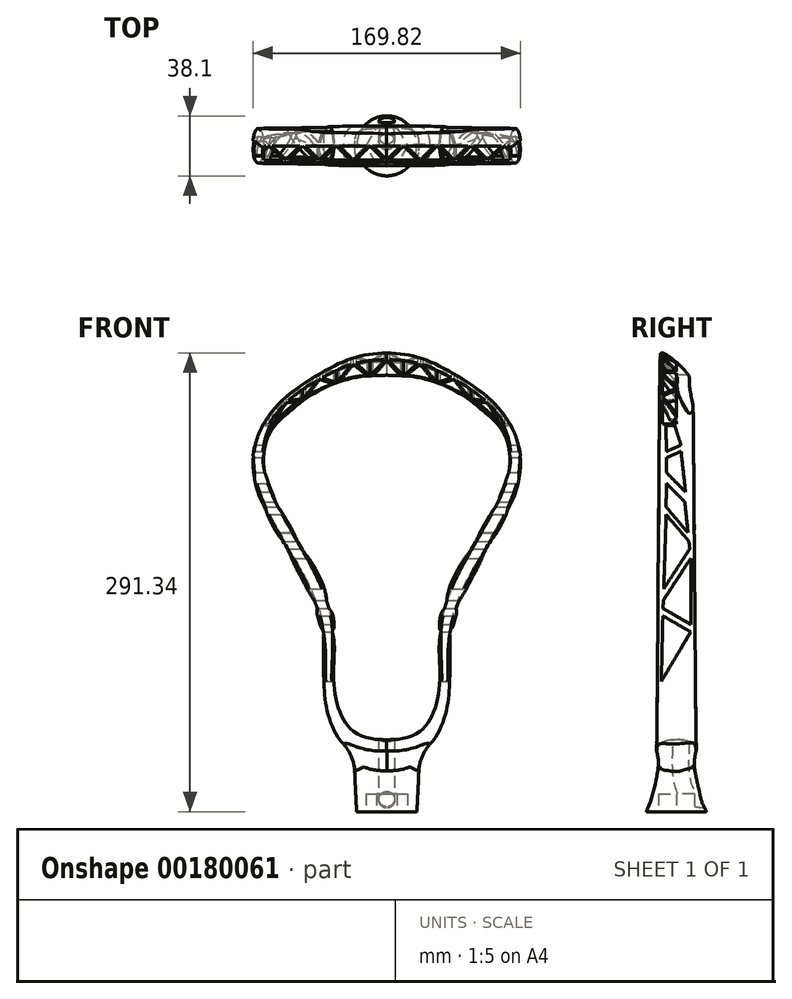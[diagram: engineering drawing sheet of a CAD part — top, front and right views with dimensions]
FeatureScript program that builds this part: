
annotation { "Feature Type Name" : "Feature", "Feature Type Description" : "" }
export const myFeature = defineFeature(function(context is Context, id is Id, definition is map)
    precondition{}
    {
        {
            var Q0;
            Q0=qCreatedBy(makeId("Front.planeOp"),FACE);
            var sketch = newSketch(context, id + "F0", { "sketchPlane" : qUnion([Q0])});
            skFitSpline(sketch, "E0", {"points": [v(0, 133.16) * mm, v(38.53, 123.96) * mm, v(74.69, 98) * mm, v(84.6, 61.8) * mm, v(62.01, 10.45) * mm, v(41.74, -37.17) * mm, v(39.37, -79) * mm, v(29.1, -107.6) * mm, v(0, -119.33) * mm], "startDerivative": vector(423.47, 0) * mm, "endDerivative": vector(-415.85, 0) * mm});
            skLineSegment(sketch, "E1", {"start": v(50.46, 17.85) * mm, "end": v(71.91, 4.1) * mm, "construction": true});
            skLineSegment(sketch, "E2", {"start": v(0, 133.16) * mm, "end": v(0, -119.33) * mm, "construction": true});
            skSolve(sketch);
        }
        {
            var Q0;
            Q0=qCreatedBy(makeId("Right.planeOp"),FACE);
            var sketch = newSketch(context, id + "F1", { "sketchPlane" : qUnion([Q0])});
            skEllipse(sketch, "E3", {"center": v(0, 128.78) * mm, "majorRadius": 14.01 * mm, "minorRadius": 3.18 * mm, "majorAxis": v(-0.7, 0.7)});
            skLineSegment(sketch, "E4", {"start": v(0, 128.78) * mm, "end": v(-9.9, 138.69) * mm, "construction": true});
            skLineSegment(sketch, "E5", {"start": v(0, 128.78) * mm, "end": v(-12.95, 128.78) * mm, "construction": true});
            skEllipse(sketch, "E6", {"center": v(0, -112.98) * mm, "majorRadius": 12.7 * mm, "minorRadius": 6.35 * mm, "majorAxis": v(1, 0)});
            skLineSegment(sketch, "E7", {"start": v(0, 140.7) * mm, "end": v(0, 110.5) * mm, "construction": true});
            skLineSegment(sketch, "E8", {"start": v(10.16, 144.05) * mm, "end": v(10.16, 100.57) * mm, "construction": true});
            skSolve(sketch);
        }
        {
            var Q0;
            Q0=sQuery(id+"F0.wireOp",EDGE,"E1");
            var Q1;
            Q1=qCreatedBy(makeId("Front.planeOp"),FACE);
            cPlane(context, id + "F2", {"entities" : qUnion([Q0, Q1]), "cplaneType" : CPlaneType.LINE_ANGLE, "offset" : 25.4 * mm, "angle" : 90 * degree, "width" : 152.4 * mm, "height" : 152.4 * mm});
        }
        {
            var Q0;
            Q0=qCreatedBy(id+"F2.planeOp",FACE);
            var sketch = newSketch(context, id + "F3", { "sketchPlane" : qUnion([Q0])});
            skEllipse(sketch, "E9", {"center": v(41.5, 0) * mm, "majorRadius": 11.43 * mm, "minorRadius": 5.08 * mm, "majorAxis": v(0, 1)});
            skSolve(sketch);
        }
        {
            var Q0;
            Q0=makeQuery(id+"F1.imprint","IMPRINT",FACE,{"disambiguationData":[TD([[makeQuery(id+"F1.imprint","IMPRINT",EDGE,{"derivedFrom":sQuery(id+"F1.wireOp",EDGE,"E3")}),1.0]])]});
            var Q1;
            Q1=makeQuery(id+"F3.imprint","IMPRINT",FACE,{"disambiguationData":[TD([[makeQuery(id+"F3.imprint","IMPRINT",EDGE,{"derivedFrom":sQuery(id+"F3.wireOp",EDGE,"E9")}),1.0]])]});
            var Q2;
            Q2=makeQuery(id+"F1.imprint","IMPRINT",FACE,{"disambiguationData":[TD([[makeQuery(id+"F1.imprint","IMPRINT",EDGE,{"derivedFrom":sQuery(id+"F1.wireOp",EDGE,"E6")}),1.0]])]});
            var Q3;
            Q3=sQuery(id+"F0.wireOp",EDGE,"E0");
            loft(context, id + "F4", {"addGuides" : true, "sheetProfilesArray" : [{ "sheetProfileEntities" : qUnion([Q0]) }, { "sheetProfileEntities" : qUnion([Q1]) }, { "sheetProfileEntities" : qUnion([Q2]) }], "guidesArray" : [{ "guideEntities" : qUnion([Q3]), "guideDerivativeType" : LoftGuideDerivativeType.DEFAULT, "guideDerivativeMagnitude" : 1 }]});
        }
        {
            var Q0;
            Q0=makeQuery(id+"F4.opLoft","SWEPT_BODY",BODY,{"disambiguationData":[OSD([sQuery(id+"F0.wireOp",EDGE,"E0"),makeQuery(id+"F1.imprint","IMPRINT",FACE,{"disambiguationData":[TD([[makeQuery(id+"F1.imprint","IMPRINT",EDGE,{"derivedFrom":sQuery(id+"F1.wireOp",EDGE,"E3")}),1.0]])]}),makeQuery(id+"F1.imprint","IMPRINT",FACE,{"disambiguationData":[TD([[makeQuery(id+"F1.imprint","IMPRINT",EDGE,{"derivedFrom":sQuery(id+"F1.wireOp",EDGE,"E6")}),1.0]])]}),sQuery(id+"F3.wireOp",EDGE,"E9")])]});
            var Q1;
            Q1=qCreatedBy(makeId("Right.planeOp"),FACE);
            mirror(context, id + "F5", {"operationType" : NewBodyOperationType.ADD, "entities" : qUnion([Q0]), "mirrorPlane" : qUnion([Q1])});
        }
        {
            var Q0;
            Q0=qCreatedBy(makeId("Front.planeOp"),FACE);
            var sketch = newSketch(context, id + "F6", { "sketchPlane" : qUnion([Q0])});
            skFitSpline(sketch, "E10", {"points": [v(-65.6, 98.25) * mm, v(-46.52, 113.2) * mm, v(-22.04, 122.89) * mm, v(0, 124.8) * mm], "startDerivative": vector(53.63, 47.73) * mm, "endDerivative": vector(67.97, 1.48) * mm});
            skFitSpline(sketch, "E11.MirrorCS", {"points": [v(65.6, 98.25) * mm, v(46.52, 113.2) * mm, v(22.04, 122.89) * mm, v(0, 124.8) * mm], "startDerivative": vector(-53.63, 47.73) * mm, "endDerivative": vector(-67.97, 1.48) * mm});
            skLineSegment(sketch, "E12", {"start": v(-65.6, 98.25) * mm, "end": v(65.6, 98.25) * mm});
            skSolve(sketch);
        }
        {
            var Q0;
            Q0 = qSketchRegion(id + "F6", true);
            extrude(context, id + "F7", {"entities" : qUnion([Q0]), "operationType" : NewBodyOperationType.REMOVE, "oppositeDirection" : true, "depth" : 45.72 * mm, "symmetric" : true});
        }
        {
            var Q0;
            Q0=makeQuery(id+"F7.boolean.opBoolean","COPY",EDGE,{"derivedFrom":makeQuery(id+"F7.opExtrude","SWEPT_EDGE",EDGE,{"disambiguationData":[OSD([sQuery(id+"F6.wireOp",EDGE,"E10"),sQuery(id+"F6.wireOp",EDGE,"E11.MirrorCS")])]})});
            fillet(context, id + "F8", {"entities" : qUnion([Q0]), "radius" : 2.54 * mm, "tangentPropagation" : true, "allowEdgeOverflow" : false});
        }
        {
            var Q0;
            Q0=qCreatedBy(makeId("Right.planeOp"),FACE);
            var sketch = newSketch(context, id + "F9", { "sketchPlane" : qUnion([Q0])});
            skLineSegment(sketch, "E13", {"start": v(-9.55, -69.61) * mm, "end": v(9.13, -38.22) * mm});
            skLineSegment(sketch, "E14", {"start": v(5.33, 44.3) * mm, "end": v(-6.29, 56.08) * mm});
            skLineSegment(sketch, "E15", {"start": v(-6.29, 56.08) * mm, "end": v(-6.55, 41.14) * mm});
            skLineSegment(sketch, "E16", {"start": v(-6.84, 24.52) * mm, "end": v(-8.04, -10.87) * mm});
            skLineSegment(sketch, "E17", {"start": v(-9.55, -69.61) * mm, "end": v(-8.63, -28.02) * mm});
            skLineSegment(sketch, "E18", {"start": v(9.13, -33.47) * mm, "end": v(9.13, 8.56) * mm});
            skLineSegment(sketch, "E19", {"start": v(5.33, 44.3) * mm, "end": v(7.4, 24.82) * mm});
            skLineSegment(sketch, "E20", {"start": v(-8.63, -28.02) * mm, "end": v(9.13, -38.22) * mm});
            skLineSegment(sketch, "E21", {"start": v(-8.47, -23.36) * mm, "end": v(9.13, -33.47) * mm});
            skLineSegment(sketch, "E22", {"start": v(-8.3, -18.19) * mm, "end": v(9.13, 8.56) * mm});
            skLineSegment(sketch, "E23", {"start": v(-8.04, -10.87) * mm, "end": v(8.5, 14.53) * mm});
            skLineSegment(sketch, "E24", {"start": v(8, 19.26) * mm, "end": v(-6.64, 36.37) * mm});
            skLineSegment(sketch, "E25", {"start": v(7.4, 24.82) * mm, "end": v(-6.55, 41.14) * mm});
            skLineSegment(sketch, "E26.trimOffspring", {"start": v(-8.3, -18.19) * mm, "end": v(-8.47, -23.36) * mm});
            skLineSegment(sketch, "E27.trimOffspring", {"start": v(8, 19.26) * mm, "end": v(8.5, 14.53) * mm});
            skLineSegment(sketch, "E28.trimOffspring", {"start": v(-6.64, 36.37) * mm, "end": v(-6.84, 24.52) * mm});
            skLineSegment(sketch, "E29", {"start": v(5.83, 50.65) * mm, "end": v(-6.29, 62.93) * mm});
            skLineSegment(sketch, "E30", {"start": v(-6.29, 62.93) * mm, "end": v(-6.29, 72.4) * mm});
            skLineSegment(sketch, "E31", {"start": v(-6.29, 72.4) * mm, "end": v(2.95, 76.46) * mm});
            skLineSegment(sketch, "E32", {"start": v(2.95, 76.46) * mm, "end": v(5.83, 50.65) * mm});
            skLineSegment(sketch, "E33", {"start": v(-6.29, 76.4) * mm, "end": v(2.95, 80.44) * mm});
            skLineSegment(sketch, "E34", {"start": v(2.95, 80.44) * mm, "end": v(-1.04, 92.76) * mm});
            skLineSegment(sketch, "E35", {"start": v(-1.04, 92.76) * mm, "end": v(-6.65, 92.76) * mm});
            skLineSegment(sketch, "E36", {"start": v(-6.65, 92.76) * mm, "end": v(-6.29, 76.4) * mm});
            skSolve(sketch);
        }
        {
            var Q0;
            Q0=makeQuery(id+"F9.imprint","IMPRINT",FACE,{"disambiguationData":[TD([[makeQuery(id+"F9.imprint","IMPRINT",EDGE,{"derivedFrom":sQuery(id+"F9.wireOp",EDGE,"E13")}),1.0]])]});
            var Q1;
            Q1=makeQuery(id+"F9.imprint","IMPRINT",FACE,{"disambiguationData":[TD([[makeQuery(id+"F9.imprint","IMPRINT",EDGE,{"derivedFrom":sQuery(id+"F9.wireOp",EDGE,"E14")}),1.0]])]});
            var Q2;
            Q2=makeQuery(id+"F9.imprint","IMPRINT",FACE,{"disambiguationData":[TD([[makeQuery(id+"F9.imprint","IMPRINT",EDGE,{"derivedFrom":sQuery(id+"F9.wireOp",EDGE,"E16")}),1.0]])]});
            var Q3;
            Q3=makeQuery(id+"F9.imprint","IMPRINT",FACE,{"disambiguationData":[TD([[makeQuery(id+"F9.imprint","IMPRINT",EDGE,{"derivedFrom":sQuery(id+"F9.wireOp",EDGE,"E18")}),1.0]])]});
            var Q4;
            Q4=makeQuery(id+"F9.imprint","IMPRINT",FACE,{"disambiguationData":[TD([[makeQuery(id+"F9.imprint","IMPRINT",EDGE,{"derivedFrom":sQuery(id+"F9.wireOp",EDGE,"E29")}),-1.0]])]});
            var Q5;
            Q5=makeQuery(id+"F9.imprint","IMPRINT",FACE,{"disambiguationData":[TD([[makeQuery(id+"F9.imprint","IMPRINT",EDGE,{"derivedFrom":sQuery(id+"F9.wireOp",EDGE,"E33")}),1.0]])]});
            var Q6;
            Q6=makeQuery(id+"F9.imprint","IMPRINT",FACE,{"disambiguationData":[TD([[makeQuery(id+"F9.imprint","IMPRINT",EDGE,{"derivedFrom":sQuery(id+"F9.wireOp",EDGE,"E13")}),1.0]])]});
            extrude(context, id + "F10", {"entities" : qUnion([Q0, Q1, Q2, Q3, Q4, Q5, Q6]), "operationType" : NewBodyOperationType.REMOVE, "oppositeDirection" : true, "depth" : 203.2 * mm, "symmetric" : true});
        }
        {
            var Q0;
            Q0=qCreatedBy(makeId("Top.planeOp"),FACE);
            cPlane(context, id + "F11", {"entities" : qUnion([Q0]), "cplaneType" : CPlaneType.OFFSET, "offset" : 152.4 * mm, "oppositeDirection" : true, "width" : 152.4 * mm, "height" : 152.4 * mm});
        }
        {
            var Q0;
            Q0=qCreatedBy(id+"F11.planeOp",FACE);
            var sketch = newSketch(context, id + "F12", { "sketchPlane" : qUnion([Q0])});
            skCircle(sketch, "E37", {"center": v(0, 0) * mm, "radius": 19.05 * mm});
            skSolve(sketch);
        }
        {
            var Q0;
            Q0=qCreatedBy(id+"F11.planeOp",FACE);
            var Q1;
            Q1=sQuery(id+"F1.wireOp",VERTEX,"E6.center");
            cPlane(context, id + "F13", {"entities" : qUnion([Q0, Q1]), "cplaneType" : CPlaneType.PLANE_POINT, "offset" : 25.4 * mm, "width" : 152.4 * mm, "height" : 152.4 * mm});
        }
        {
            var Q0;
            Q0=qCreatedBy(id+"F13.planeOp",FACE);
            var sketch = newSketch(context, id + "F14", { "sketchPlane" : qUnion([Q0])});
            skLineSegment(sketch, "E38.bottom", {"start": v(14.64, 10.24) * mm, "end": v(-14.64, 10.24) * mm});
            skLineSegment(sketch, "E38.top", {"start": v(14.64, -10.24) * mm, "end": v(-14.64, -10.24) * mm});
            skLineSegment(sketch, "E38.left", {"start": v(20.99, 3.89) * mm, "end": v(20.99, -3.89) * mm});
            skLineSegment(sketch, "E38.right", {"start": v(-20.99, 3.89) * mm, "end": v(-20.99, -3.89) * mm});
            skPoint(sketch, "E38.middle", {"position": v(0, 0) * mm});
            skPoint(sketch, "E39.visualSharp", {"position": v(-20.99, -10.24) * mm});
            skArc(sketch, "E39.filletArc", {"start": v(-20.99, -3.89) * mm, "mid": v(-19.13, -8.38) * mm, "end": v(-14.64, -10.24) * mm});
            skPoint(sketch, "E40.visualSharp", {"position": v(-20.99, 10.24) * mm});
            skArc(sketch, "E40.filletArc", {"start": v(-14.64, 10.24) * mm, "mid": v(-19.13, 8.38) * mm, "end": v(-20.99, 3.89) * mm});
            skPoint(sketch, "E41.visualSharp", {"position": v(20.99, 10.24) * mm});
            skArc(sketch, "E41.filletArc", {"start": v(20.99, 3.89) * mm, "mid": v(19.13, 8.38) * mm, "end": v(14.64, 10.24) * mm});
            skPoint(sketch, "E42.visualSharp", {"position": v(20.99, -10.24) * mm});
            skArc(sketch, "E42.filletArc", {"start": v(14.64, -10.24) * mm, "mid": v(19.13, -8.38) * mm, "end": v(20.99, -3.89) * mm});
            skSolve(sketch);
        }
        {
            var Q0;
            Q0=qCreatedBy(makeId("Right.planeOp"),FACE);
            var sketch = newSketch(context, id + "F15", { "sketchPlane" : qUnion([Q0])});
            skFitSpline(sketch, "E43", {"points": [v(-19.05, -152.4) * mm, v(-10.24, -112.98) * mm], "startDerivative": vector(12.31, 25.97) * mm, "endDerivative": vector(2.23, 40.23) * mm});
            skFitSpline(sketch, "E44.MirrorCS", {"points": [v(19.05, -152.4) * mm, v(10.24, -112.98) * mm], "startDerivative": vector(-12.31, 25.97) * mm, "endDerivative": vector(-2.23, 40.23) * mm});
            skSolve(sketch);
        }
        {
            var Q1;
            Q1=makeQuery(id+"F12.imprint","IMPRINT",FACE,{"disambiguationData":[TD([[makeQuery(id+"F12.imprint","IMPRINT",EDGE,{"derivedFrom":sQuery(id+"F12.wireOp",EDGE,"E37")}),1.0]])]});
            var Q2;
            Q2 = qSketchRegion(id + "F14", true);
            var Q3;
            Q3=sQuery(id+"F15.wireOp",EDGE,"E44.MirrorCS");
            var Q4;
            Q4=sQuery(id+"F15.wireOp",EDGE,"E43");
            loft(context, id + "F16", {"operationType" : NewBodyOperationType.ADD, "addGuides" : true, "sheetProfilesArray" : [{ "sheetProfileEntities" : qUnion([Q1]) }, { "sheetProfileEntities" : qUnion([Q2]) }], "guidesArray" : [{ "guideEntities" : qUnion([Q3]), "guideDerivativeType" : LoftGuideDerivativeType.DEFAULT, "guideDerivativeMagnitude" : 1 }, { "guideEntities" : qUnion([Q4]), "guideDerivativeType" : LoftGuideDerivativeType.DEFAULT, "guideDerivativeMagnitude" : 1 }]});
        }
        {
            var Q0;
            Q0=makeQuery(id+"F16.boolean.opBoolean","INTERSECT",EDGE,{"derivedFrom":[makeQuery(id+"F5.opPattern","COPY",FACE,{"derivedFrom":makeQuery(id+"F4.opLoft","SWEPT_FACE",FACE,{"disambiguationData":[OSD([sQuery(id+"F0.wireOp",EDGE,"E0"),sQuery(id+"F1.wireOp",EDGE,"E3"),sQuery(id+"F3.wireOp",EDGE,"E9")])]}),"instanceName":"1"}),makeQuery(id+"F16.opLoft","SWEPT_FACE",FACE,{"disambiguationData":[OSD([sQuery(id+"F12.wireOp",EDGE,"E37"),sQuery(id+"F14.wireOp",EDGE,"E38.bottom"),sQuery(id+"F14.wireOp",EDGE,"E40.filletArc"),sQuery(id+"F14.wireOp",EDGE,"E41.filletArc")])]})]});
            fillet(context, id + "F17", {"entities" : qUnion([Q0]), "radius" : 27.94 * mm, "tangentPropagation" : true, "allowEdgeOverflow" : false});
        }
        {
            var Q0;
            Q0=makeQuery(id+"F12.imprint","IMPRINT",FACE,{"disambiguationData":[TD([[makeQuery(id+"F12.imprint","IMPRINT",EDGE,{"derivedFrom":sQuery(id+"F12.wireOp",EDGE,"E37")}),1.0]])]});
            var sketch = newSketch(context, id + "F18", { "sketchPlane" : qUnion([Q0])});
            skCircle(sketch, "E45.cCircle", {"center": v(0, 0) * mm, "radius": 11.43 * mm, "construction": true});
            skLineSegment(sketch, "E45.0", {"start": v(6.6, 11.43) * mm, "end": v(13.2, 0) * mm});
            skLineSegment(sketch, "E45.1", {"start": v(13.2, 0) * mm, "end": v(6.6, -11.43) * mm});
            skLineSegment(sketch, "E45.2", {"start": v(6.6, -11.43) * mm, "end": v(-6.6, -11.43) * mm});
            skLineSegment(sketch, "E45.3", {"start": v(-6.6, -11.43) * mm, "end": v(-13.2, 0) * mm});
            skLineSegment(sketch, "E45.4", {"start": v(-13.2, 0) * mm, "end": v(-6.6, 11.43) * mm});
            skLineSegment(sketch, "E45.5", {"start": v(-6.6, 11.43) * mm, "end": v(6.6, 11.43) * mm});
            skPoint(sketch, "E45.0.midPoint", {"position": v(9.9, 5.71) * mm});
            skSolve(sketch);
        }
        {
            var Q0;
            Q0 = qSketchRegion(id + "F18", true);
            extrude(context, id + "F19", {"entities" : qUnion([Q0]), "operationType" : NewBodyOperationType.REMOVE, "depth" : 11.43 * mm});
        }
        {
            var Q0;
            Q0=qCreatedBy(makeId("Top.planeOp"),FACE);
            cPlane(context, id + "F20", {"entities" : qUnion([Q0]), "cplaneType" : CPlaneType.OFFSET, "offset" : 93.98 * mm, "width" : 152.4 * mm, "height" : 152.4 * mm});
        }
        {
            var Q0;
            Q0=qCreatedBy(id+"F20.planeOp",FACE);
            var sketch = newSketch(context, id + "F21", { "sketchPlane" : qUnion([Q0])});
            skLineSegment(sketch, "E46", {"start": v(0, -8.89) * mm, "end": v(-85.49, -8.9) * mm});
            skLineSegment(sketch, "E47", {"start": v(-85.49, -8.9) * mm, "end": v(-85.49, 0) * mm});
            skLineSegment(sketch, "E48", {"start": v(-85.49, 0) * mm, "end": v(0, 0) * mm});
            skLineSegment(sketch, "E49", {"start": v(0, 0) * mm, "end": v(0, -8.89) * mm});
            skLineSegment(sketch, "E50", {"start": v(0, -8.89) * mm, "end": v(-8.9, 0) * mm});
            skLineSegment(sketch, "E51", {"start": v(-1.8, -8.89) * mm, "end": v(-10.69, 0) * mm});
            skLineSegment(sketch, "E52", {"start": v(-12.48, 0) * mm, "end": v(-21.37, -8.89) * mm});
            skLineSegment(sketch, "E53", {"start": v(-19.58, -8.89) * mm, "end": v(-10.69, 0) * mm});
            skLineSegment(sketch, "E54.1.0.0", {"start": v(-21.37, -8.89) * mm, "end": v(-30.26, 0) * mm});
            skLineSegment(sketch, "E54.1.0.1", {"start": v(-23.17, -8.89) * mm, "end": v(-32.06, 0) * mm});
            skLineSegment(sketch, "E54.1.0.2", {"start": v(-40.95, -8.89) * mm, "end": v(-32.06, 0) * mm});
            skLineSegment(sketch, "E54.1.0.3", {"start": v(-33.85, 0) * mm, "end": v(-42.74, -8.89) * mm});
            skLineSegment(sketch, "E54.2.0.0", {"start": v(-42.74, -8.89) * mm, "end": v(-51.63, 0) * mm});
            skLineSegment(sketch, "E54.2.0.1", {"start": v(-44.54, -8.89) * mm, "end": v(-53.43, 0) * mm});
            skLineSegment(sketch, "E54.2.0.2", {"start": v(-62.32, -8.89) * mm, "end": v(-53.43, 0) * mm});
            skLineSegment(sketch, "E54.2.0.3", {"start": v(-55.23, 0) * mm, "end": v(-64.12, -8.89) * mm});
            skLineSegment(sketch, "E54.3.0.0", {"start": v(-64.11, -8.89) * mm, "end": v(-73, 0) * mm});
            skLineSegment(sketch, "E54.3.0.1", {"start": v(-65.91, -8.89) * mm, "end": v(-74.8, 0) * mm});
            skLineSegment(sketch, "E54.3.0.2", {"start": v(-83.7, -8.89) * mm, "end": v(-74.8, 0) * mm});
            skLineSegment(sketch, "E54.3.0.3", {"start": v(-76.6, 0) * mm, "end": v(-85.49, -8.89) * mm});
            skLineSegment(sketch, "E54.direction1", {"start": v(0, -8.89) * mm, "end": v(-21.37, -8.89) * mm, "construction": true});
            skLineSegment(sketch, "E55.MirrorCS", {"start": v(76.6, 0) * mm, "end": v(85.49, -8.89) * mm});
            skLineSegment(sketch, "E56.MirrorCS", {"start": v(64.11, -8.89) * mm, "end": v(73, 0) * mm});
            skLineSegment(sketch, "E57.MirrorCS", {"start": v(83.7, -8.89) * mm, "end": v(74.8, 0) * mm});
            skLineSegment(sketch, "E58.MirrorCS", {"start": v(0, -8.89) * mm, "end": v(21.37, -8.89) * mm, "construction": true});
            skLineSegment(sketch, "E59.MirrorCS", {"start": v(42.74, -8.89) * mm, "end": v(51.63, 0) * mm});
            skLineSegment(sketch, "E60.MirrorCS", {"start": v(33.85, 0) * mm, "end": v(42.74, -8.89) * mm});
            skLineSegment(sketch, "E61.MirrorCS", {"start": v(40.95, -8.89) * mm, "end": v(32.06, 0) * mm});
            skLineSegment(sketch, "E62.MirrorCS", {"start": v(23.17, -8.89) * mm, "end": v(32.06, 0) * mm});
            skLineSegment(sketch, "E63.MirrorCS", {"start": v(21.37, -8.89) * mm, "end": v(30.26, 0) * mm});
            skLineSegment(sketch, "E64.MirrorCS", {"start": v(0, -8.89) * mm, "end": v(85.49, -8.89) * mm});
            skLineSegment(sketch, "E65.MirrorCS", {"start": v(19.58, -8.89) * mm, "end": v(10.69, 0) * mm});
            skLineSegment(sketch, "E66.MirrorCS", {"start": v(62.32, -8.89) * mm, "end": v(53.43, 0) * mm});
            skLineSegment(sketch, "E67.MirrorCS", {"start": v(44.54, -8.89) * mm, "end": v(53.43, 0) * mm});
            skLineSegment(sketch, "E68.MirrorCS", {"start": v(0, -8.89) * mm, "end": v(8.9, 0) * mm});
            skLineSegment(sketch, "E69.MirrorCS", {"start": v(1.8, -8.89) * mm, "end": v(10.69, 0) * mm});
            skLineSegment(sketch, "E70.MirrorCS", {"start": v(12.48, 0) * mm, "end": v(21.37, -8.89) * mm});
            skLineSegment(sketch, "E71.MirrorCS", {"start": v(65.91, -8.89) * mm, "end": v(74.8, 0) * mm});
            skLineSegment(sketch, "E72.MirrorCS", {"start": v(55.23, 0) * mm, "end": v(64.12, -8.89) * mm});
            skLineSegment(sketch, "E73.MirrorCS", {"start": v(85.49, 0) * mm, "end": v(0, 0) * mm});
            skLineSegment(sketch, "E74.MirrorCS", {"start": v(85.49, -8.9) * mm, "end": v(85.49, 0) * mm});
            skSolve(sketch);
        }
        {
            var Q0;
            {var subQ0=sQuery(id+"F21.wireOp",EDGE,"E49");Q0=makeQuery(id+"F21.imprint","IMPRINT",FACE,{"disambiguationData":[TD([[makeQuery(id+"F21.imprint","IMPRINT",EDGE,{"derivedFrom":subQ0}),-1.0]])]});}
            var Q1;
            {var subQ0=sQuery(id+"F21.wireOp",EDGE,"E51");Q1=makeQuery(id+"F21.imprint","IMPRINT",FACE,{"disambiguationData":[TD([[makeQuery(id+"F21.imprint","IMPRINT",EDGE,{"derivedFrom":subQ0}),1.0]])]});}
            var Q2;
            {var subQ0=sQuery(id+"F21.wireOp",EDGE,"E52");var subQ1=sQuery(id+"F21.wireOp",EDGE,"E48");var subQ2=makeQuery(id+"F21.imprint","INTERSECT",VERTEX,{"derivedFrom":[subQ1,subQ0]});Q2=makeQuery(id+"F21.imprint","IMPRINT",FACE,{"disambiguationData":[TD([[makeQuery(id+"F21.imprint","IMPRINT",EDGE,{"disambiguationData":[TD([[subQ2,1.0]])],"derivedFrom":subQ1}),-1.0]])]});}
            var Q3;
            {var subQ0=sQuery(id+"F21.wireOp",EDGE,"E54.1.0.1");Q3=makeQuery(id+"F21.imprint","IMPRINT",FACE,{"disambiguationData":[TD([[makeQuery(id+"F21.imprint","IMPRINT",EDGE,{"derivedFrom":subQ0}),1.0]])]});}
            var Q4;
            {var subQ0=sQuery(id+"F21.wireOp",EDGE,"E54.1.0.3");var subQ1=sQuery(id+"F21.wireOp",EDGE,"E48");var subQ2=makeQuery(id+"F21.imprint","INTERSECT",VERTEX,{"derivedFrom":[subQ1,subQ0]});Q4=makeQuery(id+"F21.imprint","IMPRINT",FACE,{"disambiguationData":[TD([[makeQuery(id+"F21.imprint","IMPRINT",EDGE,{"disambiguationData":[TD([[subQ2,1.0]])],"derivedFrom":subQ1}),-1.0]])]});}
            var Q5;
            {var subQ0=sQuery(id+"F21.wireOp",EDGE,"E54.2.0.1");Q5=makeQuery(id+"F21.imprint","IMPRINT",FACE,{"disambiguationData":[TD([[makeQuery(id+"F21.imprint","IMPRINT",EDGE,{"derivedFrom":subQ0}),1.0]])]});}
            var Q6;
            {var subQ0=sQuery(id+"F21.wireOp",EDGE,"E54.2.0.3");var subQ1=sQuery(id+"F21.wireOp",EDGE,"E48");var subQ2=makeQuery(id+"F21.imprint","INTERSECT",VERTEX,{"derivedFrom":[subQ1,subQ0]});Q6=makeQuery(id+"F21.imprint","IMPRINT",FACE,{"disambiguationData":[TD([[makeQuery(id+"F21.imprint","IMPRINT",EDGE,{"disambiguationData":[TD([[subQ2,1.0]])],"derivedFrom":subQ1}),-1.0]])]});}
            var Q7;
            {var subQ0=sQuery(id+"F21.wireOp",EDGE,"E54.3.0.1");Q7=makeQuery(id+"F21.imprint","IMPRINT",FACE,{"disambiguationData":[TD([[makeQuery(id+"F21.imprint","IMPRINT",EDGE,{"derivedFrom":subQ0}),1.0]])]});}
            var Q8;
            {var subQ0=sQuery(id+"F21.wireOp",EDGE,"E47");Q8=makeQuery(id+"F21.imprint","IMPRINT",FACE,{"disambiguationData":[TD([[makeQuery(id+"F21.imprint","IMPRINT",EDGE,{"derivedFrom":subQ0}),-1.0]])]});}
            var Q9;
            {var subQ0=sQuery(id+"F21.wireOp",EDGE,"E49");Q9=makeQuery(id+"F21.imprint","IMPRINT",FACE,{"disambiguationData":[TD([[makeQuery(id+"F21.imprint","IMPRINT",EDGE,{"derivedFrom":subQ0}),1.0]])]});}
            var Q10;
            {var subQ0=sQuery(id+"F21.wireOp",EDGE,"E65.MirrorCS");Q10=makeQuery(id+"F21.imprint","IMPRINT",FACE,{"disambiguationData":[TD([[makeQuery(id+"F21.imprint","IMPRINT",EDGE,{"derivedFrom":subQ0}),1.0]])]});}
            var Q11;
            {var subQ0=sQuery(id+"F21.wireOp",EDGE,"E73.MirrorCS");var subQ1=sQuery(id+"F21.wireOp",EDGE,"E63.MirrorCS");var subQ2=makeQuery(id+"F21.imprint","INTERSECT",VERTEX,{"derivedFrom":[subQ1,subQ0]});Q11=makeQuery(id+"F21.imprint","IMPRINT",FACE,{"disambiguationData":[TD([[makeQuery(id+"F21.imprint","IMPRINT",EDGE,{"disambiguationData":[TD([[subQ2,1.0]])],"derivedFrom":subQ1}),1.0]])]});}
            var Q12;
            {var subQ0=sQuery(id+"F21.wireOp",EDGE,"E61.MirrorCS");Q12=makeQuery(id+"F21.imprint","IMPRINT",FACE,{"disambiguationData":[TD([[makeQuery(id+"F21.imprint","IMPRINT",EDGE,{"derivedFrom":subQ0}),1.0]])]});}
            var Q13;
            {var subQ0=sQuery(id+"F21.wireOp",EDGE,"E73.MirrorCS");var subQ1=sQuery(id+"F21.wireOp",EDGE,"E59.MirrorCS");var subQ2=makeQuery(id+"F21.imprint","INTERSECT",VERTEX,{"derivedFrom":[subQ1,subQ0]});Q13=makeQuery(id+"F21.imprint","IMPRINT",FACE,{"disambiguationData":[TD([[makeQuery(id+"F21.imprint","IMPRINT",EDGE,{"disambiguationData":[TD([[subQ2,1.0]])],"derivedFrom":subQ1}),1.0]])]});}
            var Q14;
            {var subQ0=sQuery(id+"F21.wireOp",EDGE,"E66.MirrorCS");Q14=makeQuery(id+"F21.imprint","IMPRINT",FACE,{"disambiguationData":[TD([[makeQuery(id+"F21.imprint","IMPRINT",EDGE,{"derivedFrom":subQ0}),1.0]])]});}
            var Q15;
            {var subQ0=sQuery(id+"F21.wireOp",EDGE,"E73.MirrorCS");var subQ1=sQuery(id+"F21.wireOp",EDGE,"E56.MirrorCS");var subQ2=makeQuery(id+"F21.imprint","INTERSECT",VERTEX,{"derivedFrom":[subQ1,subQ0]});Q15=makeQuery(id+"F21.imprint","IMPRINT",FACE,{"disambiguationData":[TD([[makeQuery(id+"F21.imprint","IMPRINT",EDGE,{"disambiguationData":[TD([[subQ2,1.0]])],"derivedFrom":subQ1}),1.0]])]});}
            var Q16;
            {var subQ0=sQuery(id+"F21.wireOp",EDGE,"E57.MirrorCS");Q16=makeQuery(id+"F21.imprint","IMPRINT",FACE,{"disambiguationData":[TD([[makeQuery(id+"F21.imprint","IMPRINT",EDGE,{"derivedFrom":subQ0}),1.0]])]});}
            var Q17;
            {var subQ0=sQuery(id+"F21.wireOp",EDGE,"E55.MirrorCS");Q17=makeQuery(id+"F21.imprint","IMPRINT",FACE,{"disambiguationData":[TD([[makeQuery(id+"F21.imprint","IMPRINT",EDGE,{"derivedFrom":subQ0}),1.0]])]});}
            extrude(context, id + "F22", {"entities" : qUnion([Q0, Q1, Q2, Q3, Q4, Q5, Q6, Q7, Q8, Q9, Q10, Q11, Q12, Q13, Q14, Q15, Q16, Q17]), "operationType" : NewBodyOperationType.REMOVE, "depth" : 55.88 * mm});
        }
        {
            var Q0;
            Q0=qCreatedBy(makeId("Right.planeOp"),FACE);
            var sketch = newSketch(context, id + "F23", { "sketchPlane" : qUnion([Q0])});
            skFitSpline(sketch, "E75", {"points": [v(3.67, -101.66) * mm, v(3.31, -130.79) * mm, v(9.35, -143.04) * mm, v(22.85, -145.07) * mm], "startDerivative": vector(-5.61, -74.54) * mm, "endDerivative": vector(52.39, 0) * mm});
            skSolve(sketch);
        }
        {
            var Q0;
            Q0=sQuery(id+"F23.wireOp",VERTEX,"E75.end");
            var Q1;
            Q1=qCreatedBy(makeId("Front.planeOp"),FACE);
            cPlane(context, id + "F24", {"entities" : qUnion([Q0, Q1]), "cplaneType" : CPlaneType.PLANE_POINT, "offset" : 25.4 * mm, "width" : 152.4 * mm, "height" : 152.4 * mm});
        }
        {
            var Q0;
            Q0=qCreatedBy(id+"F24.planeOp",FACE);
            var sketch = newSketch(context, id + "F25", { "sketchPlane" : qUnion([Q0])});
            skCircle(sketch, "E76", {"center": v(0, -145.07) * mm, "radius": 5.08 * mm});
            skSolve(sketch);
        }
        {
            var Q0;
            Q0=makeQuery(id+"F25.imprint","IMPRINT",FACE,{"disambiguationData":[TD([[makeQuery(id+"F25.imprint","IMPRINT",EDGE,{"derivedFrom":sQuery(id+"F25.wireOp",EDGE,"E76")}),1.0]])]});
            var Q1;
            Q1=sQuery(id+"F23.wireOp",EDGE,"E75");
            sweep(context, id + "F26", {"operationType" : NewBodyOperationType.REMOVE, "profiles" : qUnion([Q0]), "path" : qUnion([Q1])});
        }
    });
